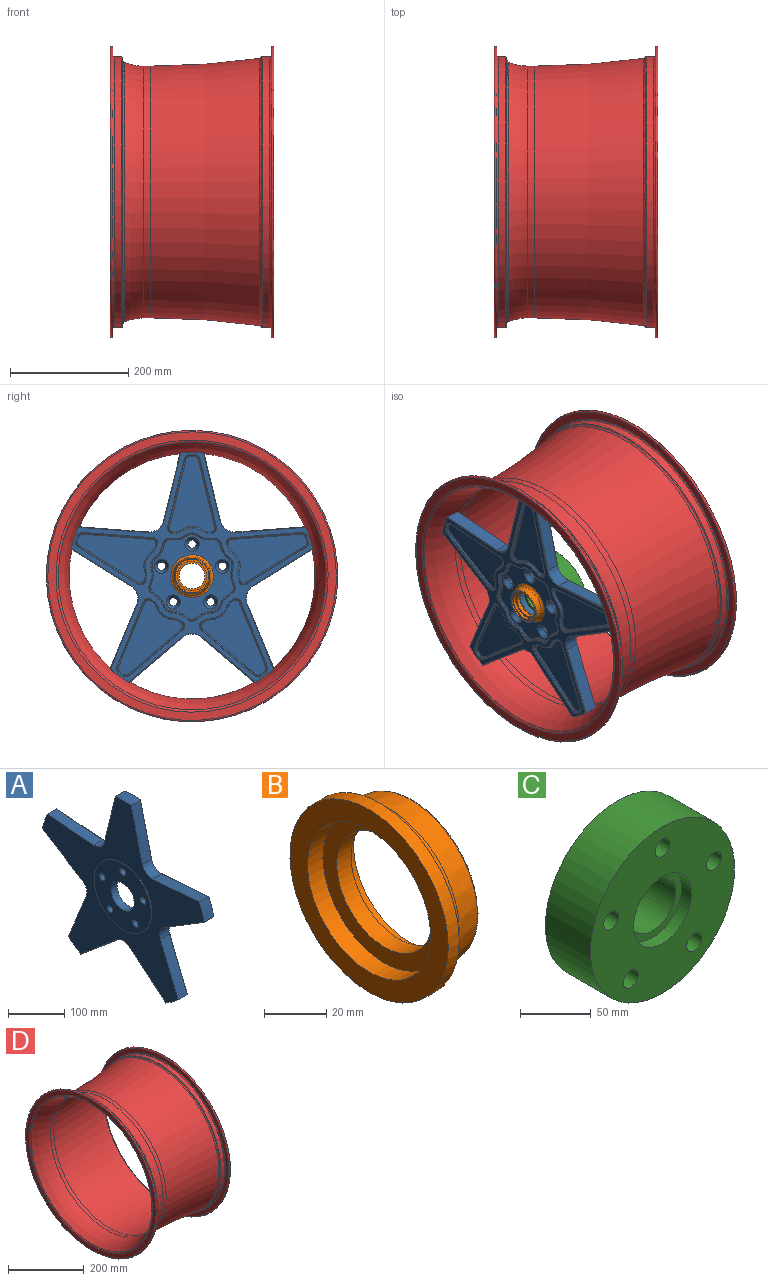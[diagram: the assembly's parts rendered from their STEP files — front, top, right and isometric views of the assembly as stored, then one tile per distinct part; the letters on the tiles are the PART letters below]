
ASSEMBLY  parts=4 mates=7
PART A: 331 faces, bbox 25.4x408.7x389.3 mm
  f0: cylinder r=29mm len=58mm, axis (-1,0,0), area 2806.1mm2, adj f129,f330
  f1: plane 407.61x388.53mm, normal (1,0,0), area 16823.9mm2, adj f102,f105,f108,f111,f126,f224,f225,f226
  f2: torus R=23mm, axis (1,0,0), area 45.1mm2, adj f3,f4,f18,f26
  f3: cylinder r=2mm len=3.32mm, axis (0,0.31,-0.95), area 8.9mm2, adj f2,f5,f24,f26
  f4: torus R=30mm, axis (1,0,0), area 106.7mm2, adj f2,f6,f23,f26
  f5: torus R=6mm, axis (1,0,0), area 41.3mm2, adj f3,f7,f15,f26
  f6: torus R=23mm, axis (1,0,0), area 45.1mm2, adj f4,f8,f19,f26
  f7: cylinder r=2mm len=101.73mm, axis (0,0.85,0.53), area 371.7mm2, adj f5,f9,f25,f26
  f8: cylinder r=2mm len=3.32mm, axis (0,0.31,-0.95), area 8.9mm2, adj f6,f10,f22,f26
  f9: torus R=6mm, axis (1,0,0), area 29.9mm2, adj f7,f11,f14,f26
  f10: torus R=6mm, axis (1,0,0), area 41.3mm2, adj f8,f12,f16,f26
  f11: torus R=202mm, axis (1,0,0), area 28.8mm2, adj f9,f13,f20,f26
  f12: cylinder r=2mm len=118.12mm, axis (0,-1,-0.08), area 371.7mm2, adj f10,f13,f21,f26
  f13: torus R=6mm, axis (1,0,0), area 29.9mm2, adj f11,f12,f17,f26
  f14: cylinder r=8mm len=9.11mm, axis (1,0,0), area 21mm2, adj f9,f20,f25,f259
  f15: cylinder r=8mm len=11.81mm, axis (-1,0,0), area 29mm2, adj f5,f24,f25,f263
  f16: cylinder r=8mm len=10.45mm, axis (-1,0,0), area 29mm2, adj f10,f21,f22,f256
  f17: cylinder r=8mm len=8.15mm, axis (1,0,0), area 21mm2, adj f13,f20,f21,f255
  f18: cylinder r=25mm len=14.57mm, axis (1,0,0), area 29.6mm2, adj f2,f23,f24,f264
  f19: cylinder r=25mm len=11.94mm, axis (1,0,0), area 29.6mm2, adj f6,f22,f23,f260
  f20: cylinder r=204mm len=8.74mm, axis (1,0,0), area 18.4mm2, adj f11,f14,f17,f257
  f21: plane 117.97x8.92mm, normal (0,0.08,-1), area 236.6mm2, adj f12,f16,f17,f254
  f22: plane 2.7x2mm, normal (0,0.95,0.31), area 5.7mm2, adj f8,f16,f19,f258
  f23: cylinder r=28mm len=29.69mm, axis (1,0,0), area 66.2mm2, adj f4,f18,f19,f262
  f24: plane 2.7x2mm, normal (0,0.95,0.31), area 5.7mm2, adj f3,f15,f18,f265
  f25: plane 100.68x62.12mm, normal (0,-0.53,0.85), area 236.6mm2, adj f7,f14,f15,f261
  f26: plane 132.7x82.52mm, normal (1,0,0), area 5926.3mm2, adj f2,f3,f4,f5,f6,f7,f8,f9
  f27: torus R=23mm, axis (1,0,0), area 45.1mm2, adj f28,f29,f43,f51
  f28: cylinder r=2mm len=3.47mm, axis (0,-0.81,-0.59), area 8.9mm2, adj f27,f30,f49,f51
  f29: torus R=30mm, axis (1,0,0), area 106.7mm2, adj f27,f31,f48,f51
  f30: torus R=6mm, axis (1,0,0), area 41.3mm2, adj f28,f32,f40,f51
  f31: torus R=23mm, axis (1,0,0), area 45.1mm2, adj f29,f33,f44,f51
  f32: cylinder r=2mm len=91.49mm, axis (0,0.76,-0.65), area 371.7mm2, adj f30,f34,f50,f51
  f33: cylinder r=2mm len=3.47mm, axis (0,-0.81,-0.59), area 8.9mm2, adj f31,f35,f47,f51
  f34: torus R=6mm, axis (1,0,0), area 29.9mm2, adj f32,f36,f39,f51
  f35: torus R=6mm, axis (1,0,0), area 41.3mm2, adj f33,f37,f41,f51
  f36: torus R=202mm, axis (1,0,0), area 28.8mm2, adj f34,f38,f45,f51
  f37: cylinder r=2mm len=110.2mm, axis (0,-0.38,0.93), area 371.7mm2, adj f35,f38,f46,f51
  f38: torus R=6mm, axis (1,0,0), area 29.9mm2, adj f36,f37,f42,f51
  f39: cylinder r=8mm len=9.73mm, axis (1,0,0), area 21mm2, adj f34,f45,f50,f271
  f40: cylinder r=8mm len=12.57mm, axis (-1,0,0), area 29mm2, adj f30,f49,f50,f267
  f41: cylinder r=8mm len=12.1mm, axis (-1,0,0), area 29mm2, adj f35,f46,f47,f276
  f42: cylinder r=8mm len=9.4mm, axis (1,0,0), area 21mm2, adj f38,f45,f46,f275
  f43: cylinder r=25mm len=13.77mm, axis (1,0,0), area 29.6mm2, adj f27,f48,f49,f268
  f44: cylinder r=25mm len=11.63mm, axis (1,0,0), area 29.6mm2, adj f31,f47,f48,f272
  f45: cylinder r=204mm len=7.44mm, axis (1,0,0), area 18.4mm2, adj f36,f39,f42,f273
  f46: plane 109.44x44.94mm, normal (0,-0.93,-0.38), area 236.6mm2, adj f37,f41,f42,f277
  f47: plane 2.3x2mm, normal (0,0.59,-0.81), area 5.7mm2, adj f33,f41,f44,f274
  f48: cylinder r=28mm len=25.26mm, axis (1,0,0), area 66.2mm2, adj f29,f43,f44,f270
  f49: plane 2.3x2mm, normal (0,0.59,-0.81), area 5.7mm2, adj f28,f40,f43,f266
  f50: plane 90.19x76.56mm, normal (0,0.65,0.76), area 236.6mm2, adj f32,f39,f40,f269
  f51: plane 126.63x109.34mm, normal (1,0,0), area 5926.3mm2, adj f27,f28,f29,f30,f31,f32,f33,f34
  f52: torus R=23mm, axis (1,0,0), area 45.1mm2, adj f53,f54,f68,f76
  f53: cylinder r=2mm len=3.47mm, axis (0,-0.81,0.59), area 8.9mm2, adj f52,f55,f74,f76
  f54: torus R=30mm, axis (1,0,0), area 106.7mm2, adj f52,f56,f73,f76
  f55: torus R=6mm, axis (1,0,0), area 41.3mm2, adj f53,f57,f65,f76
  f56: torus R=23mm, axis (1,0,0), area 45.1mm2, adj f54,f58,f69,f76
  f57: cylinder r=2mm len=110.2mm, axis (0,-0.38,-0.93), area 371.7mm2, adj f55,f59,f75,f76
  f58: cylinder r=2mm len=3.47mm, axis (0,-0.81,0.59), area 8.9mm2, adj f56,f60,f72,f76
  f59: torus R=6mm, axis (1,0,0), area 29.9mm2, adj f57,f61,f64,f76
  f60: torus R=6mm, axis (1,0,0), area 41.3mm2, adj f58,f62,f66,f76
  f61: torus R=202mm, axis (1,0,0), area 28.8mm2, adj f59,f63,f70,f76
  f62: cylinder r=2mm len=91.49mm, axis (0,0.76,0.65), area 371.7mm2, adj f60,f63,f71,f76
  f63: torus R=6mm, axis (1,0,0), area 29.9mm2, adj f61,f62,f67,f76
  f64: cylinder r=8mm len=9.4mm, axis (1,0,0), area 21mm2, adj f59,f70,f75,f279
  f65: cylinder r=8mm len=12.1mm, axis (-1,0,0), area 29mm2, adj f55,f74,f75,f280
  f66: cylinder r=8mm len=12.57mm, axis (-1,0,0), area 29mm2, adj f60,f71,f72,f287
  f67: cylinder r=8mm len=9.73mm, axis (1,0,0), area 21mm2, adj f63,f70,f71,f283
  f68: cylinder r=25mm len=11.63mm, axis (1,0,0), area 29.6mm2, adj f52,f73,f74,f284
  f69: cylinder r=25mm len=13.77mm, axis (1,0,0), area 29.6mm2, adj f56,f72,f73,f288
  f70: cylinder r=204mm len=7.44mm, axis (1,0,0), area 18.4mm2, adj f61,f64,f67,f281
  f71: plane 90.19x76.56mm, normal (0,-0.65,0.76), area 236.6mm2, adj f62,f66,f67,f285
  f72: plane 2.3x2mm, normal (0,-0.59,-0.81), area 5.7mm2, adj f58,f66,f69,f289
  f73: cylinder r=28mm len=25.26mm, axis (1,0,0), area 66.2mm2, adj f54,f68,f69,f286
  f74: plane 2.3x2mm, normal (0,-0.59,-0.81), area 5.7mm2, adj f53,f65,f68,f282
  f75: plane 109.44x44.94mm, normal (0,0.93,-0.38), area 236.6mm2, adj f57,f64,f65,f278
  f76: plane 126.63x109.34mm, normal (1,0,0), area 5926.3mm2, adj f52,f53,f54,f55,f56,f57,f58,f59
  f77: torus R=23mm, axis (1,0,0), area 45.1mm2, adj f78,f79,f93,f101
  f78: cylinder r=2mm len=3.32mm, axis (0,0.31,0.95), area 8.9mm2, adj f77,f80,f99,f101
  f79: torus R=30mm, axis (1,0,0), area 106.7mm2, adj f77,f81,f98,f101
  f80: torus R=6mm, axis (1,0,0), area 41.3mm2, adj f78,f82,f90,f101
  f81: torus R=23mm, axis (1,0,0), area 45.1mm2, adj f79,f83,f94,f101
  f82: cylinder r=2mm len=118.12mm, axis (0,-1,0.08), area 371.7mm2, adj f80,f84,f100,f101
  f83: cylinder r=2mm len=3.32mm, axis (0,0.31,0.95), area 8.9mm2, adj f81,f85,f97,f101
  f84: torus R=6mm, axis (1,0,0), area 29.9mm2, adj f82,f86,f89,f101
  f85: torus R=6mm, axis (1,0,0), area 41.3mm2, adj f83,f87,f91,f101
  f86: torus R=202mm, axis (1,0,0), area 28.8mm2, adj f84,f88,f95,f101
  f87: cylinder r=2mm len=101.73mm, axis (0,0.85,-0.53), area 371.7mm2, adj f85,f88,f96,f101
  f88: torus R=6mm, axis (1,0,0), area 29.9mm2, adj f86,f87,f92,f101
  f89: cylinder r=8mm len=8.15mm, axis (1,0,0), area 21mm2, adj f84,f95,f100,f291
  f90: cylinder r=8mm len=10.45mm, axis (-1,0,0), area 29mm2, adj f80,f99,f100,f292
  f91: cylinder r=8mm len=11.81mm, axis (-1,0,0), area 29mm2, adj f85,f96,f97,f299
  f92: cylinder r=8mm len=9.11mm, axis (1,0,0), area 21mm2, adj f88,f95,f96,f295
  f93: cylinder r=25mm len=11.94mm, axis (1,0,0), area 29.6mm2, adj f77,f98,f99,f296
  f94: cylinder r=25mm len=14.57mm, axis (1,0,0), area 29.6mm2, adj f81,f97,f98,f300
  f95: cylinder r=204mm len=8.74mm, axis (1,0,0), area 18.4mm2, adj f86,f89,f92,f293
  f96: plane 100.68x62.12mm, normal (0,0.53,0.85), area 236.6mm2, adj f87,f91,f92,f297
  f97: plane 2.7x2mm, normal (0,-0.95,0.31), area 5.7mm2, adj f83,f91,f94,f301
  f98: cylinder r=28mm len=29.69mm, axis (1,0,0), area 66.2mm2, adj f79,f93,f94,f298
  f99: plane 2.7x2mm, normal (0,-0.95,0.31), area 5.7mm2, adj f78,f90,f93,f294
  f100: plane 117.97x8.92mm, normal (0,-0.08,-1), area 236.6mm2, adj f82,f89,f90,f290
  f101: plane 132.7x82.52mm, normal (1,0,0), area 5926.3mm2, adj f77,f78,f79,f80,f81,f82,f83,f84
  f102: cylinder r=209mm len=32.36mm, axis (-1,0,0), area 960.8mm2, adj f1,f104,f106,f127,f168,f316,f317
  f103: plane 100.38x61.94mm, normal (0,0.53,-0.85), area 2712.9mm2, adj f126,f127,f161,f314
  f104: plane 109.11x44.81mm, normal (0,0.93,0.38), area 2712.9mm2, adj f102,f127,f161,f316
  f105: cylinder r=209mm len=32.36mm, axis (-1,0,0), area 960.8mm2, adj f1,f107,f109,f127,f166,f319,f320
  f106: plane 89.92x76.33mm, normal (0,-0.65,-0.76), area 2595mm2, adj f102,f162,f168,f317
  f107: plane 89.92x76.33mm, normal (0,0.65,-0.76), area 2595mm2, adj f105,f162,f166,f319
  f108: cylinder r=209mm len=38.04mm, axis (-1,0,0), area 961mm2, adj f1,f110,f112,f127,f322,f323
  f109: plane 109.11x44.81mm, normal (0,-0.93,0.38), area 2712.9mm2, adj f105,f127,f163,f320
  f110: plane 100.38x61.94mm, normal (0,-0.53,-0.85), area 2712.9mm2, adj f108,f127,f163,f322
  f111: cylinder r=209mm len=40mm, axis (-1,0,0), area 961mm2, adj f1,f113,f127,f134,f325,f326
  f112: plane 117.62x23mm, normal (0,0.08,1), area 2712.9mm2, adj f108,f127,f164,f323
  f113: plane 114.61x27.88mm, normal (0,-0.97,0.24), area 2712.9mm2, adj f111,f127,f164,f325
  f114: cylinder r=18mm len=22.13mm, axis (-1,0,0), area 50.6mm2, adj f192,f193,f214,f243
  f115: cone r=7mm half-angle=30deg, axis (1,0,0), area 596.9mm2, adj f116,f131
  f116: cylinder r=7mm len=14mm, axis (-1,0,0), area 516.3mm2, adj f115,f129
  f117: cylinder r=18mm len=18.82mm, axis (-1,0,0), area 50.6mm2, adj f190,f191,f221,f252
  f118: cone r=7mm half-angle=30deg, axis (1,0,0), area 596.9mm2, adj f119,f131
  f119: cylinder r=7mm len=14mm, axis (-1,0,0), area 516.3mm2, adj f118,f129
  f120: cylinder r=18mm len=18.82mm, axis (-1,0,0), area 50.6mm2, adj f188,f189,f209,f240
  f121: cone r=7mm half-angle=30deg, axis (1,0,0), area 596.9mm2, adj f122,f131
  f122: cylinder r=7mm len=14mm, axis (-1,0,0), area 516.3mm2, adj f121,f129
  f123: cylinder r=18mm len=22.13mm, axis (-1,0,0), area 50.6mm2, adj f186,f187,f197,f228
  f124: cone r=7mm half-angle=30deg, axis (1,0,0), area 596.9mm2, adj f125,f131
  f125: cylinder r=7mm len=14mm, axis (-1,0,0), area 516.3mm2, adj f124,f129
  f126: cylinder r=209mm len=38.04mm, axis (-1,0,0), area 961mm2, adj f1,f103,f127,f135,f314,f328
  f127: plane 408.08x388.53mm, normal (-1,0,0), area 52573.4mm2, adj f102,f103,f104,f105,f108,f109,f110,f111
  f128: cylinder r=72mm len=144mm, axis (-1,0,0), area 633.3mm2, adj f127,f129
  f129: plane 144x144mm, normal (-1,0,0), area 12874.2mm2, adj f0,f116,f119,f122,f125,f128,f133
  f130: cylinder r=18mm len=23.26mm, axis (-1,0,0), area 50.6mm2, adj f184,f185,f202,f231
  f131: plane 143.04x139.91mm, normal (1,0,0), area 8175.5mm2, adj f115,f118,f121,f124,f132,f194,f195,f196
  f132: cone r=7mm half-angle=30deg, axis (1,0,0), area 596.9mm2, adj f131,f133
  f133: cylinder r=7mm len=14mm, axis (-1,0,0), area 516.3mm2, adj f129,f132
  f134: plane 114.61x27.88mm, normal (0,0.97,0.24), area 2712.9mm2, adj f111,f127,f165,f326
  f135: plane 117.62x23mm, normal (0,-0.08,1), area 2712.9mm2, adj f126,f127,f165,f328
  f136: cylinder r=204mm len=9.19mm, axis (1,0,0), area 18.4mm2, adj f145,f148,f158,f305
  f137: plane 114.95x27.97mm, normal (0,0.97,-0.24), area 236.6mm2, adj f145,f146,f159,f309
  f138: plane 2.84x2mm, normal (0,0,1), area 5.7mm2, adj f143,f146,f155,f313
  f139: cylinder r=28mm len=31.22mm, axis (1,0,0), area 66.2mm2, adj f143,f144,f151,f310
  f140: plane 2.84x2mm, normal (0,0,1), area 5.7mm2, adj f144,f147,f150,f306
  f141: plane 114.95x27.97mm, normal (0,-0.97,-0.24), area 236.6mm2, adj f147,f148,f154,f302
  f142: plane 127x76.77mm, normal (1,0,0), area 5926.3mm2, adj f149,f150,f151,f152,f153,f154,f155,f156
  f143: cylinder r=25mm len=13.94mm, axis (1,0,0), area 29.6mm2, adj f138,f139,f153,f312
  f144: cylinder r=25mm len=13.94mm, axis (1,0,0), area 29.6mm2, adj f139,f140,f149,f308
  f145: cylinder r=8mm len=7.59mm, axis (1,0,0), area 21mm2, adj f136,f137,f160,f307
  f146: cylinder r=8mm len=9.89mm, axis (-1,0,0), area 29mm2, adj f137,f138,f157,f311
  f147: cylinder r=8mm len=9.89mm, axis (-1,0,0), area 29mm2, adj f140,f141,f152,f304
  f148: cylinder r=8mm len=7.59mm, axis (1,0,0), area 21mm2, adj f136,f141,f156,f303
  f149: torus R=23mm, axis (1,0,0), area 45.1mm2, adj f142,f144,f150,f151
  f150: cylinder r=2mm len=2.84mm, axis (0,1,0), area 8.9mm2, adj f140,f142,f149,f152
  f151: torus R=30mm, axis (1,0,0), area 106.7mm2, adj f139,f142,f149,f153
  f152: torus R=6mm, axis (1,0,0), area 41.3mm2, adj f142,f147,f150,f154
  f153: torus R=23mm, axis (1,0,0), area 45.1mm2, adj f142,f143,f151,f155
  f154: cylinder r=2mm len=115.42mm, axis (0,-0.24,0.97), area 371.7mm2, adj f141,f142,f152,f156
  f155: cylinder r=2mm len=2.84mm, axis (0,1,0), area 8.9mm2, adj f138,f142,f153,f157
  f156: torus R=6mm, axis (1,0,0), area 29.9mm2, adj f142,f148,f154,f158
  f157: torus R=6mm, axis (1,0,0), area 41.3mm2, adj f142,f146,f155,f159
  f158: torus R=202mm, axis (1,0,0), area 28.8mm2, adj f136,f142,f156,f160
  f159: cylinder r=2mm len=115.42mm, axis (0,-0.24,-0.97), area 371.7mm2, adj f137,f142,f157,f160
  f160: torus R=6mm, axis (1,0,0), area 29.9mm2, adj f142,f145,f158,f159
  f161: cylinder r=25mm len=30.77mm, axis (1,0,0), area 809.4mm2, adj f103,f104,f127,f315
  f162: cylinder r=25mm len=32.36mm, axis (1,0,0), area 774.2mm2, adj f106,f107,f167,f318
  f163: cylinder r=25mm len=30.77mm, axis (1,0,0), area 809.4mm2, adj f109,f110,f127,f321
  f164: cylinder r=25mm len=26.18mm, axis (1,0,0), area 809.4mm2, adj f112,f113,f127,f324
  f165: cylinder r=25mm len=26.18mm, axis (1,0,0), area 809.4mm2, adj f127,f134,f135,f327
  f166: cylinder r=1mm len=90.83mm, axis (0,-0.76,-0.65), area 185.5mm2, adj f105,f107,f127,f167
  f167: torus R=26mm, axis (1,0,0), area 56.1mm2, adj f127,f162,f166,f168
  f168: cylinder r=1mm len=90.83mm, axis (0,-0.76,0.65), area 185.5mm2, adj f102,f106,f127,f167
  f169: plane 12.5x2mm, normal (0,0,-1), area 25mm2, adj f179,f184,f198,f227
  f170: plane 11.89x3.86mm, normal (0,0.95,-0.31), area 25mm2, adj f179,f187,f194,f224
  f171: plane 11.89x3.86mm, normal (0,0.95,-0.31), area 25mm2, adj f180,f186,f201,f232
  f172: plane 10.11x7.35mm, normal (0,0.59,0.81), area 25mm2, adj f180,f189,f205,f236
  f173: plane 10.11x7.35mm, normal (0,0.59,0.81), area 25mm2, adj f181,f188,f213,f244
  f174: plane 10.11x7.35mm, normal (0,-0.59,0.81), area 25mm2, adj f181,f191,f217,f248
  f175: plane 10.11x7.35mm, normal (0,-0.59,0.81), area 25mm2, adj f182,f190,f222,f251
  f176: plane 11.89x3.86mm, normal (0,-0.95,-0.31), area 25mm2, adj f182,f193,f218,f247
  f177: plane 11.89x3.86mm, normal (0,-0.95,-0.31), area 25mm2, adj f183,f192,f210,f239
  f178: plane 12.5x2mm, normal (0,0,-1), area 25mm2, adj f183,f185,f206,f235
  f179: cylinder r=12mm len=11.41mm, axis (1,0,0), area 30.2mm2, adj f169,f170,f196,f225
  f180: cylinder r=12mm len=13.42mm, axis (1,0,0), area 30.2mm2, adj f171,f172,f203,f234
  f181: cylinder r=12mm len=14.11mm, axis (1,0,0), area 30.2mm2, adj f173,f174,f215,f246
  f182: cylinder r=12mm len=13.42mm, axis (1,0,0), area 30.2mm2, adj f175,f176,f220,f249
  f183: cylinder r=12mm len=11.41mm, axis (1,0,0), area 30.2mm2, adj f177,f178,f208,f237
  f184: cylinder r=20mm len=12.92mm, axis (-1,0,0), area 28.1mm2, adj f130,f169,f200,f229
  f185: cylinder r=20mm len=12.92mm, axis (-1,0,0), area 28.1mm2, adj f130,f178,f204,f233
  f186: cylinder r=20mm len=13.76mm, axis (-1,0,0), area 28.1mm2, adj f123,f171,f199,f230
  f187: cylinder r=20mm len=10.83mm, axis (-1,0,0), area 28.1mm2, adj f123,f170,f195,f226
  f188: cylinder r=20mm len=13.24mm, axis (-1,0,0), area 28.1mm2, adj f120,f173,f211,f242
  f189: cylinder r=20mm len=11.43mm, axis (-1,0,0), area 28.1mm2, adj f120,f172,f207,f238
  f190: cylinder r=20mm len=11.43mm, axis (-1,0,0), area 28.1mm2, adj f117,f175,f223,f253
  f191: cylinder r=20mm len=13.24mm, axis (-1,0,0), area 28.1mm2, adj f117,f174,f219,f250
  f192: cylinder r=20mm len=10.83mm, axis (-1,0,0), area 28.1mm2, adj f114,f177,f212,f241
  f193: cylinder r=20mm len=13.76mm, axis (-1,0,0), area 28.1mm2, adj f114,f176,f216,f245
  f194: cylinder r=2mm len=12.5mm, axis (0,0.31,0.95), area 39.3mm2, adj f131,f170,f195,f196
  f195: torus R=22mm, axis (-1,0,0), area 45.8mm2, adj f131,f187,f194,f197
  f196: torus R=10mm, axis (-1,0,0), area 44.5mm2, adj f131,f179,f194,f198
  f197: torus R=16mm, axis (-1,0,0), area 76.3mm2, adj f123,f131,f195,f199
  f198: cylinder r=2mm len=12.5mm, axis (0,1,0), area 39.3mm2, adj f131,f169,f196,f200
  f199: torus R=22mm, axis (-1,0,0), area 45.8mm2, adj f131,f186,f197,f201
  f200: torus R=22mm, axis (-1,0,0), area 45.8mm2, adj f131,f184,f198,f202
  f201: cylinder r=2mm len=12.5mm, axis (0,0.31,0.95), area 39.3mm2, adj f131,f171,f199,f203
  f202: torus R=16mm, axis (-1,0,0), area 76.3mm2, adj f130,f131,f200,f204
  f203: torus R=10mm, axis (-1,0,0), area 44.5mm2, adj f131,f180,f201,f205
  f204: torus R=22mm, axis (-1,0,0), area 45.8mm2, adj f131,f185,f202,f206
  f205: cylinder r=2mm len=11.29mm, axis (0,-0.81,0.59), area 39.3mm2, adj f131,f172,f203,f207
  f206: cylinder r=2mm len=12.5mm, axis (0,1,0), area 39.3mm2, adj f131,f178,f204,f208
  f207: torus R=22mm, axis (-1,0,0), area 45.8mm2, adj f131,f189,f205,f209
  f208: torus R=10mm, axis (-1,0,0), area 44.5mm2, adj f131,f183,f206,f210
  f209: torus R=16mm, axis (-1,0,0), area 76.3mm2, adj f120,f131,f207,f211
  f210: cylinder r=2mm len=12.5mm, axis (0,0.31,-0.95), area 39.3mm2, adj f131,f177,f208,f212
  f211: torus R=22mm, axis (-1,0,0), area 45.8mm2, adj f131,f188,f209,f213
  f212: torus R=22mm, axis (-1,0,0), area 45.8mm2, adj f131,f192,f210,f214
  f213: cylinder r=2mm len=11.29mm, axis (0,-0.81,0.59), area 39.3mm2, adj f131,f173,f211,f215
  f214: torus R=16mm, axis (-1,0,0), area 76.3mm2, adj f114,f131,f212,f216
  f215: torus R=10mm, axis (-1,0,0), area 44.5mm2, adj f131,f181,f213,f217
  f216: torus R=22mm, axis (-1,0,0), area 45.8mm2, adj f131,f193,f214,f218
  f217: cylinder r=2mm len=11.29mm, axis (0,-0.81,-0.59), area 39.3mm2, adj f131,f174,f215,f219
  f218: cylinder r=2mm len=12.5mm, axis (0,0.31,-0.95), area 39.3mm2, adj f131,f176,f216,f220
  f219: torus R=22mm, axis (-1,0,0), area 45.8mm2, adj f131,f191,f217,f221
  f220: torus R=10mm, axis (-1,0,0), area 44.5mm2, adj f131,f182,f218,f222
  f221: torus R=16mm, axis (-1,0,0), area 76.3mm2, adj f117,f131,f219,f223
  f222: cylinder r=2mm len=11.29mm, axis (0,-0.81,-0.59), area 39.3mm2, adj f131,f175,f220,f223
  f223: torus R=22mm, axis (-1,0,0), area 45.8mm2, adj f131,f190,f221,f222
  f224: cylinder r=1mm len=12.2mm, axis (0,-0.31,-0.95), area 19.6mm2, adj f1,f170,f225,f226
  f225: torus R=13mm, axis (-1,0,0), area 24.4mm2, adj f1,f179,f224,f227
  f226: torus R=19mm, axis (-1,0,0), area 21.7mm2, adj f1,f187,f224,f228
  f227: cylinder r=1mm len=12.5mm, axis (0,-1,0), area 19.6mm2, adj f1,f169,f225,f229
  f228: torus R=19mm, axis (-1,0,0), area 40.5mm2, adj f1,f123,f226,f230
  f229: torus R=19mm, axis (-1,0,0), area 21.7mm2, adj f1,f184,f227,f231
  f230: torus R=19mm, axis (-1,0,0), area 21.7mm2, adj f1,f186,f228,f232
  f231: torus R=19mm, axis (-1,0,0), area 40.5mm2, adj f1,f130,f229,f233
  f232: cylinder r=1mm len=12.2mm, axis (0,-0.31,-0.95), area 19.6mm2, adj f1,f171,f230,f234
  f233: torus R=19mm, axis (-1,0,0), area 21.7mm2, adj f1,f185,f231,f235
  f234: torus R=13mm, axis (-1,0,0), area 24.4mm2, adj f1,f180,f232,f236
  f235: cylinder r=1mm len=12.5mm, axis (0,-1,0), area 19.6mm2, adj f1,f178,f233,f237
  f236: cylinder r=1mm len=10.7mm, axis (0,0.81,-0.59), area 19.6mm2, adj f1,f172,f234,f238
  f237: torus R=13mm, axis (-1,0,0), area 24.4mm2, adj f1,f183,f235,f239
  f238: torus R=19mm, axis (-1,0,0), area 21.7mm2, adj f1,f189,f236,f240
  f239: cylinder r=1mm len=12.2mm, axis (0,-0.31,0.95), area 19.6mm2, adj f1,f177,f237,f241
  f240: torus R=19mm, axis (-1,0,0), area 40.5mm2, adj f1,f120,f238,f242
  f241: torus R=19mm, axis (-1,0,0), area 21.7mm2, adj f1,f192,f239,f243
  f242: torus R=19mm, axis (-1,0,0), area 21.7mm2, adj f1,f188,f240,f244
  f243: torus R=19mm, axis (-1,0,0), area 40.5mm2, adj f1,f114,f241,f245
  f244: cylinder r=1mm len=10.7mm, axis (0,0.81,-0.59), area 19.6mm2, adj f1,f173,f242,f246
  f245: torus R=19mm, axis (-1,0,0), area 21.7mm2, adj f1,f193,f243,f247
  f246: torus R=13mm, axis (-1,0,0), area 24.4mm2, adj f1,f181,f244,f248
  f247: cylinder r=1mm len=12.2mm, axis (0,-0.31,0.95), area 19.6mm2, adj f1,f176,f245,f249
  f248: cylinder r=1mm len=10.7mm, axis (0,0.81,0.59), area 19.6mm2, adj f1,f174,f246,f250
  f249: torus R=13mm, axis (-1,0,0), area 24.4mm2, adj f1,f182,f247,f251
  f250: torus R=19mm, axis (-1,0,0), area 21.7mm2, adj f1,f191,f248,f252
  f251: cylinder r=1mm len=10.7mm, axis (0,0.81,0.59), area 19.6mm2, adj f1,f175,f249,f253
  f252: torus R=19mm, axis (-1,0,0), area 40.5mm2, adj f1,f117,f250,f253
  f253: torus R=19mm, axis (-1,0,0), area 21.7mm2, adj f1,f190,f251,f252
  f254: cylinder r=1mm len=118.04mm, axis (0,-1,-0.08), area 185.8mm2, adj f1,f21,f255,f256
  f255: torus R=9mm, axis (-1,0,0), area 17.2mm2, adj f1,f17,f254,f257
  f256: torus R=9mm, axis (-1,0,0), area 23.8mm2, adj f1,f16,f254,f258
  f257: torus R=205mm, axis (-1,0,0), area 14.5mm2, adj f1,f20,f255,f259
  f258: cylinder r=1mm len=3.01mm, axis (0,0.31,-0.95), area 4.5mm2, adj f1,f22,f256,f260
  f259: torus R=9mm, axis (-1,0,0), area 17.2mm2, adj f1,f14,f257,f261
  f260: torus R=26mm, axis (-1,0,0), area 23.6mm2, adj f1,f19,f258,f262
  f261: cylinder r=1mm len=101.21mm, axis (0,0.85,0.53), area 185.8mm2, adj f1,f25,f259,f263
  f262: torus R=27mm, axis (-1,0,0), area 51.3mm2, adj f1,f23,f260,f264
  f263: torus R=9mm, axis (-1,0,0), area 23.8mm2, adj f1,f15,f261,f265
  f264: torus R=26mm, axis (-1,0,0), area 23.6mm2, adj f1,f18,f262,f265
  f265: cylinder r=1mm len=3.01mm, axis (0,0.31,-0.95), area 4.5mm2, adj f1,f24,f263,f264
  f266: cylinder r=1mm len=2.88mm, axis (0,-0.81,-0.59), area 4.5mm2, adj f1,f49,f267,f268
  f267: torus R=9mm, axis (-1,0,0), area 23.8mm2, adj f1,f40,f266,f269
  f268: torus R=26mm, axis (-1,0,0), area 23.6mm2, adj f1,f43,f266,f270
  f269: cylinder r=1mm len=90.84mm, axis (0,0.76,-0.65), area 185.8mm2, adj f1,f50,f267,f271
  f270: torus R=27mm, axis (-1,0,0), area 51.3mm2, adj f1,f48,f268,f272
  f271: torus R=9mm, axis (-1,0,0), area 17.2mm2, adj f1,f39,f269,f273
  f272: torus R=26mm, axis (-1,0,0), area 23.6mm2, adj f1,f44,f270,f274
  f273: torus R=205mm, axis (-1,0,0), area 14.5mm2, adj f1,f45,f271,f275
  f274: cylinder r=1mm len=2.88mm, axis (0,-0.81,-0.59), area 4.5mm2, adj f1,f47,f272,f276
  f275: torus R=9mm, axis (-1,0,0), area 17.2mm2, adj f1,f42,f273,f277
  f276: torus R=9mm, axis (-1,0,0), area 23.8mm2, adj f1,f41,f274,f277
  f277: cylinder r=1mm len=109.82mm, axis (0,-0.38,0.93), area 185.8mm2, adj f1,f46,f275,f276
  f278: cylinder r=1mm len=109.82mm, axis (0,-0.38,-0.93), area 185.8mm2, adj f1,f75,f279,f280
  f279: torus R=9mm, axis (-1,0,0), area 17.2mm2, adj f1,f64,f278,f281
  f280: torus R=9mm, axis (-1,0,0), area 23.8mm2, adj f1,f65,f278,f282
  f281: torus R=205mm, axis (-1,0,0), area 14.5mm2, adj f1,f70,f279,f283
  f282: cylinder r=1mm len=2.88mm, axis (0,-0.81,0.59), area 4.5mm2, adj f1,f74,f280,f284
  f283: torus R=9mm, axis (-1,0,0), area 17.2mm2, adj f1,f67,f281,f285
  f284: torus R=26mm, axis (-1,0,0), area 23.6mm2, adj f1,f68,f282,f286
  f285: cylinder r=1mm len=90.84mm, axis (0,0.76,0.65), area 185.8mm2, adj f1,f71,f283,f287
  f286: torus R=27mm, axis (-1,0,0), area 51.3mm2, adj f1,f73,f284,f288
  f287: torus R=9mm, axis (-1,0,0), area 23.8mm2, adj f1,f66,f285,f289
  f288: torus R=26mm, axis (-1,0,0), area 23.6mm2, adj f1,f69,f286,f289
  f289: cylinder r=1mm len=2.88mm, axis (0,-0.81,0.59), area 4.5mm2, adj f1,f72,f287,f288
  f290: cylinder r=1mm len=118.04mm, axis (0,-1,0.08), area 185.8mm2, adj f1,f100,f291,f292
  f291: torus R=9mm, axis (-1,0,0), area 17.2mm2, adj f1,f89,f290,f293
  f292: torus R=9mm, axis (-1,0,0), area 23.8mm2, adj f1,f90,f290,f294
  f293: torus R=205mm, axis (-1,0,0), area 14.5mm2, adj f1,f95,f291,f295
  f294: cylinder r=1mm len=3.01mm, axis (0,0.31,0.95), area 4.5mm2, adj f1,f99,f292,f296
  f295: torus R=9mm, axis (-1,0,0), area 17.2mm2, adj f1,f92,f293,f297
  f296: torus R=26mm, axis (-1,0,0), area 23.6mm2, adj f1,f93,f294,f298
  f297: cylinder r=1mm len=101.21mm, axis (0,0.85,-0.53), area 185.8mm2, adj f1,f96,f295,f299
  f298: torus R=27mm, axis (-1,0,0), area 51.3mm2, adj f1,f98,f296,f300
  f299: torus R=9mm, axis (-1,0,0), area 23.8mm2, adj f1,f91,f297,f301
  f300: torus R=26mm, axis (-1,0,0), area 23.6mm2, adj f1,f94,f298,f301
  f301: cylinder r=1mm len=3.01mm, axis (0,0.31,0.95), area 4.5mm2, adj f1,f97,f299,f300
  f302: cylinder r=1mm len=115.19mm, axis (0,-0.24,0.97), area 185.8mm2, adj f1,f141,f303,f304
  f303: torus R=9mm, axis (-1,0,0), area 17.2mm2, adj f1,f148,f302,f305
  f304: torus R=9mm, axis (-1,0,0), area 23.8mm2, adj f1,f147,f302,f306
  f305: torus R=205mm, axis (-1,0,0), area 14.5mm2, adj f1,f136,f303,f307
  f306: cylinder r=1mm len=2.84mm, axis (0,1,0), area 4.5mm2, adj f1,f140,f304,f308
  f307: torus R=9mm, axis (-1,0,0), area 17.2mm2, adj f1,f145,f305,f309
  f308: torus R=26mm, axis (-1,0,0), area 23.6mm2, adj f1,f144,f306,f310
  f309: cylinder r=1mm len=115.19mm, axis (0,-0.24,-0.97), area 185.8mm2, adj f1,f137,f307,f311
  f310: torus R=27mm, axis (-1,0,0), area 51.3mm2, adj f1,f139,f308,f312
  f311: torus R=9mm, axis (-1,0,0), area 23.8mm2, adj f1,f146,f309,f313
  f312: torus R=26mm, axis (-1,0,0), area 23.6mm2, adj f1,f143,f310,f313
  f313: cylinder r=1mm len=2.84mm, axis (0,1,0), area 4.5mm2, adj f1,f138,f311,f312
  f314: cylinder r=1mm len=101.2mm, axis (0,0.85,0.53), area 185.5mm2, adj f1,f103,f126,f315
  f315: torus R=26mm, axis (-1,0,0), area 56.1mm2, adj f1,f161,f314,f316
  f316: cylinder r=1mm len=109.81mm, axis (0,-0.38,0.93), area 185.5mm2, adj f1,f102,f104,f315
  f317: cylinder r=1mm len=90.83mm, axis (0,0.76,-0.65), area 185.5mm2, adj f1,f102,f106,f318
  f318: torus R=26mm, axis (-1,0,0), area 56.1mm2, adj f1,f162,f317,f319
  f319: cylinder r=1mm len=90.83mm, axis (0,0.76,0.65), area 185.5mm2, adj f1,f105,f107,f318
  f320: cylinder r=1mm len=109.81mm, axis (0,-0.38,-0.93), area 185.5mm2, adj f1,f105,f109,f321
  f321: torus R=26mm, axis (-1,0,0), area 56.1mm2, adj f1,f163,f320,f322
  f322: cylinder r=1mm len=101.2mm, axis (0,0.85,-0.53), area 185.5mm2, adj f1,f108,f110,f321
  f323: cylinder r=1mm len=118.04mm, axis (0,-1,0.08), area 185.5mm2, adj f1,f108,f112,f324
  f324: torus R=26mm, axis (-1,0,0), area 56.1mm2, adj f1,f164,f323,f325
  f325: cylinder r=1mm len=115.18mm, axis (0,-0.24,-0.97), area 185.5mm2, adj f1,f111,f113,f324
  f326: cylinder r=1mm len=115.18mm, axis (0,-0.24,0.97), area 185.5mm2, adj f1,f111,f134,f327
  f327: torus R=26mm, axis (-1,0,0), area 56.1mm2, adj f1,f165,f326,f328
  f328: cylinder r=1mm len=118.04mm, axis (0,-1,-0.08), area 185.5mm2, adj f1,f126,f135,f327
  f329: cylinder r=36mm len=72mm, axis (1,0,0), area 1131mm2, adj f131,f330
  f330: plane 72x72mm, normal (1,0,0), area 1429.4mm2, adj f0,f329
PART B: 13 faces, bbox 20x79.8x79.8 mm
  f0: cylinder r=25mm len=50mm, axis (1,0,0), area 706.9mm2, adj f8,f10
  f1: cylinder r=21.72mm len=43.43mm, axis (-1,0,0), area 886.9mm2, adj f7,f8
  f2: plane 58.32x58.32mm, normal (1,0,0), area 208.5mm2, adj f9,f12
  f3: cone r=30mm half-angle=10deg, axis (-1,0,0), area 2003mm2, adj f11,f12
  f4: cylinder r=36mm len=72mm, axis (-1,0,0), area 1131mm2, adj f5,f11
  f5: plane 72x72mm, normal (-1,0,0), area 1608.5mm2, adj f4,f6
  f6: cylinder r=28mm len=56mm, axis (-1,0,0), area 1231.5mm2, adj f5,f7
  f7: plane 56x56mm, normal (-1,0,0), area 981.3mm2, adj f1,f6
  f8: plane 50x50mm, normal (1,0,0), area 481.8mm2, adj f0,f1
  f9: cylinder r=28mm len=56mm, axis (1,0,0), area 351.9mm2, adj f2,f10
  f10: plane 56x56mm, normal (1,0,0), area 499.5mm2, adj f0,f9
  f11: torus R=36.85mm, axis (-1,0,0), area 1290.5mm2, adj f3,f4
  f12: torus R=29.16mm, axis (-1,0,0), area 261mm2, adj f2,f3
PART C: 14 faces, bbox 144x50x144 mm
  f0: cylinder r=23mm len=46mm, axis (0,-1,0), area 5780.5mm2, adj f10,f12
  f1: cylinder r=7.5mm len=45mm, axis (0,-1,0), area 2120.6mm2, adj f6,f7
  f2: cylinder r=7.5mm len=45mm, axis (0,-1,0), area 2120.6mm2, adj f6,f7
  f3: cylinder r=7.5mm len=45mm, axis (0,-1,0), area 2120.6mm2, adj f6,f7
  f4: cylinder r=7.5mm len=45mm, axis (0,-1,0), area 2120.6mm2, adj f6,f7
  f5: cylinder r=72mm len=144mm, axis (0,1,0), area 20357.5mm2, adj f6,f7
  f6: plane 144x144mm, normal (0,-1,0), area 12760.4mm2, adj f1,f2,f3,f4,f5,f8,f9
  f7: plane 144x144mm, normal (0,1,0), area 11876.8mm2, adj f1,f2,f3,f4,f5,f8,f11
  f8: cylinder r=7.5mm len=45mm, axis (0,-1,0), area 2120.6mm2, adj f6,f7
  f9: cylinder r=29mm len=58mm, axis (0,-1,0), area 1822.1mm2, adj f6,f10
  f10: plane 58x58mm, normal (0,-1,0), area 980.2mm2, adj f0,f9
  f11: cylinder r=33.5mm len=67mm, axis (0,-1,0), area 631.5mm2, adj f7,f13
  f12: plane 63x63mm, normal (0,1,0), area 1455.3mm2, adj f0,f13
  f13: torus R=31.5mm, axis (0,1,0), area 646.9mm2, adj f11,f12
PART D: 23 faces, bbox 1003.6x1276.5x1276.5 mm
  f0: torus R=243.6mm, axis (-1,0,0), area 12099.7mm2, adj f1,f14
  f1: plane 487.2x487.2mm, normal (-1,0,0), area 20578.1mm2, adj f0,f15
  f2: torus R=299.84mm, axis (-1,0,0), area 79033.2mm2, adj f3,f15
  f3: cylinder r=207.6mm len=415.2mm, axis (-1,0,0), area 14855mm2, adj f2,f4
  f4: torus R=1512.83mm, axis (-1,0,0), area 274266mm2, adj f3,f16
  f5: plane 487.2x487.2mm, normal (1,0,0), area 22251.9mm2, adj f6,f16
  f6: torus R=243.6mm, axis (-1,0,0), area 12099.7mm2, adj f5,f7
  f7: plane 487.2x487.2mm, normal (-1,0,0), area 19366.7mm2, adj f6,f19
  f8: cylinder r=228.6mm len=457.2mm, axis (-1,0,0), area 18423.7mm2, adj f19,f20
  f9: torus R=1512.83mm, axis (-1,0,0), area 250897.7mm2, adj f10,f17
  f10: cylinder r=212.6mm len=425.2mm, axis (-1,0,0), area 15212.8mm2, adj f9,f11
  f11: torus R=299.84mm, axis (-1,0,0), area 45436.6mm2, adj f10,f18
  f12: plane 453.2x453.2mm, normal (1,0,0), area 4171.9mm2, adj f18,f21
  f13: cylinder r=228.6mm len=457.2mm, axis (-1,0,0), area 17236mm2, adj f21,f22
  f14: plane 487.2x487.2mm, normal (1,0,0), area 19366.7mm2, adj f0,f22
  f15: torus R=229.76mm, axis (-1,0,0), area 6669.4mm2, adj f1,f2
  f16: torus R=228.6mm, axis (-1,0,0), area 10020.6mm2, adj f4,f5
  f17: torus R=230.56mm, axis (-1,0,0), area 5892.9mm2, adj f9,f20
  f18: torus R=223.65mm, axis (-1,0,0), area 8226.8mm2, adj f11,f12
  f19: torus R=230.6mm, axis (1,0,0), area 4526.7mm2, adj f7,f8
  f20: torus R=226.6mm, axis (1,0,0), area 2782.8mm2, adj f8,f17
  f21: torus R=226.6mm, axis (1,0,0), area 4498mm2, adj f12,f13
  f22: torus R=230.6mm, axis (1,0,0), area 4526.7mm2, adj f13,f14
PLACE A rot(axis=(0,-0.95,-0.31),180deg) t=(551.7,182.34,-77.86)mm
PLACE B rot(axis=(0,0.31,-0.95),180deg) t=(536.3,182.34,-77.86)mm
PLACE C rot(axis=(0,0,1),90deg) t=(551.7,182.34,-77.86)mm
PLACE D rot(axis=(1,0,0),36deg) t=(642.05,182.34,-77.86)mm
MATE planar A.f329 <-> B.f9  axis (-1,0,0) through (536.3,182.34,-77.86)mm
MATE cylindrical C.f0 <-> A.f0  axis (1,0,0) through (566.7,182.34,-77.86)mm
MATE planar A.f329 <-> C.f5  axis (1,0,0) through (551.7,182.34,-77.86)mm
MATE planar C.f1 <-> D.f0  axis (1,0,0) through (596.7,130.98,-61.18)mm
MATE slider A.f0 <-> D.f0  axis (1,0,0) through (551.7,182.34,-77.86)mm
MATE cylindrical A.f4 <-> C.f4  axis (1,0,0) through (539.96,233.7,-61.18)mm
MATE cylindrical B.f1 <-> A.f329  axis (1,0,0) through (533.8,182.34,-77.86)mm
